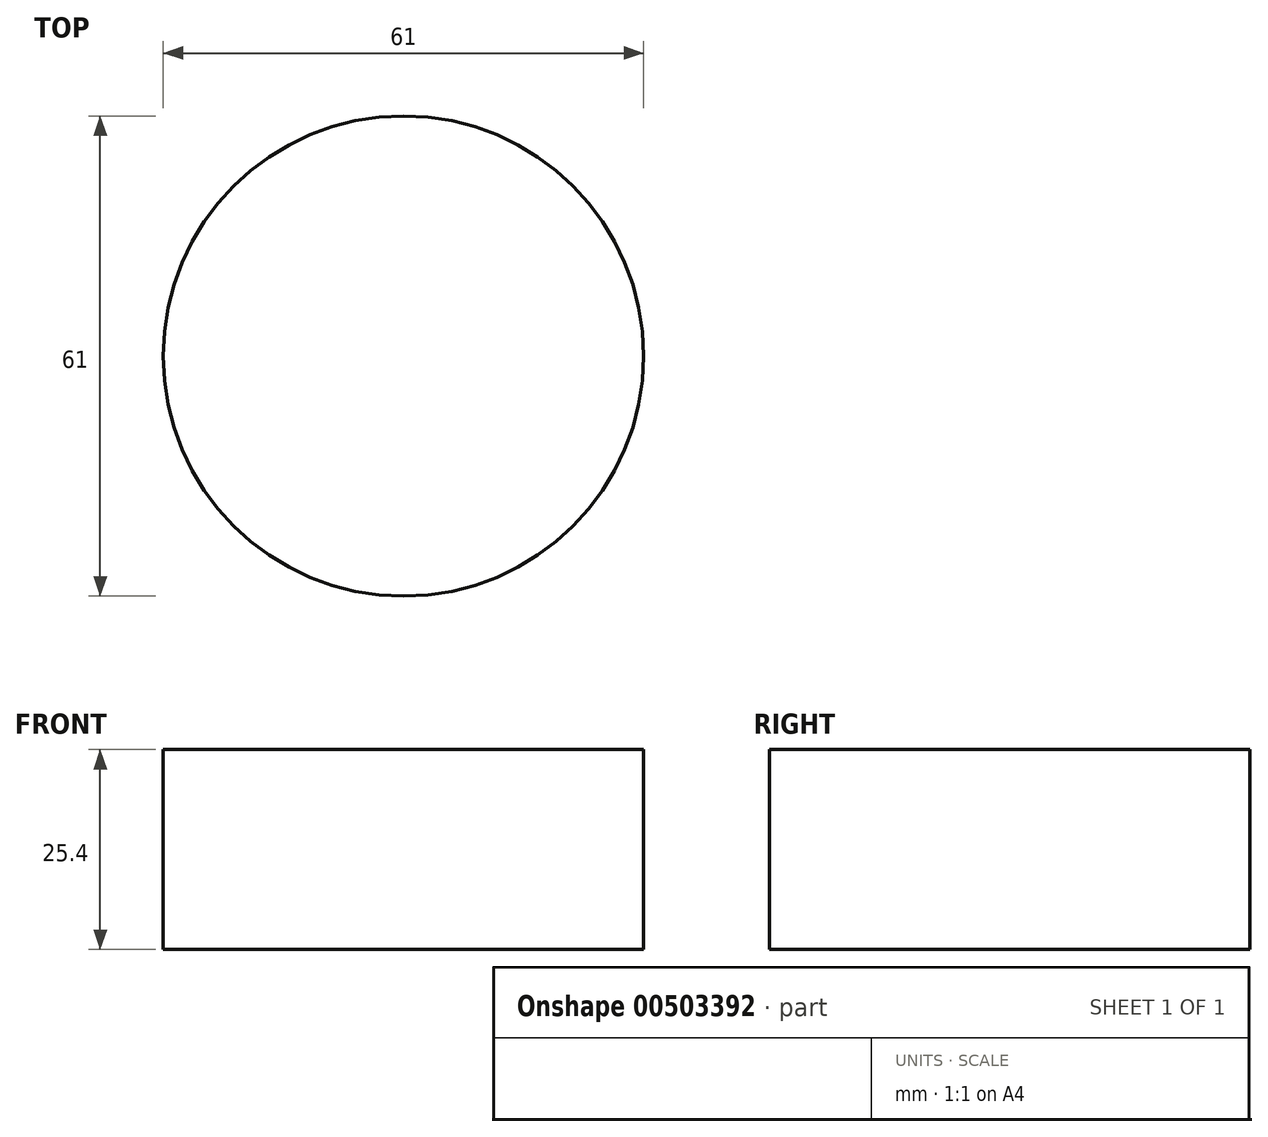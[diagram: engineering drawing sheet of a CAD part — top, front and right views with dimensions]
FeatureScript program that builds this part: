
annotation { "Feature Type Name" : "Feature", "Feature Type Description" : "" }
export const myFeature = defineFeature(function(context is Context, id is Id, definition is map)
    precondition{}
    {
        {
            var Q0;
            Q0=qCreatedBy(makeId("Top.planeOp"),FACE);
            var sketch = newSketch(context, id + "F0", { "sketchPlane" : qUnion([Q0])});
            skCircle(sketch, "E0", {"center": v(0, 0) * mm, "radius": 30.5 * mm});
            skSolve(sketch);
        }
        {
            var Q0;
            Q0 = qSketchRegion(id + "F0", true);
            extrude(context, id + "F1", {"entities" : qUnion([Q0]), "depth" : 25.4 * mm});
        }
    });
